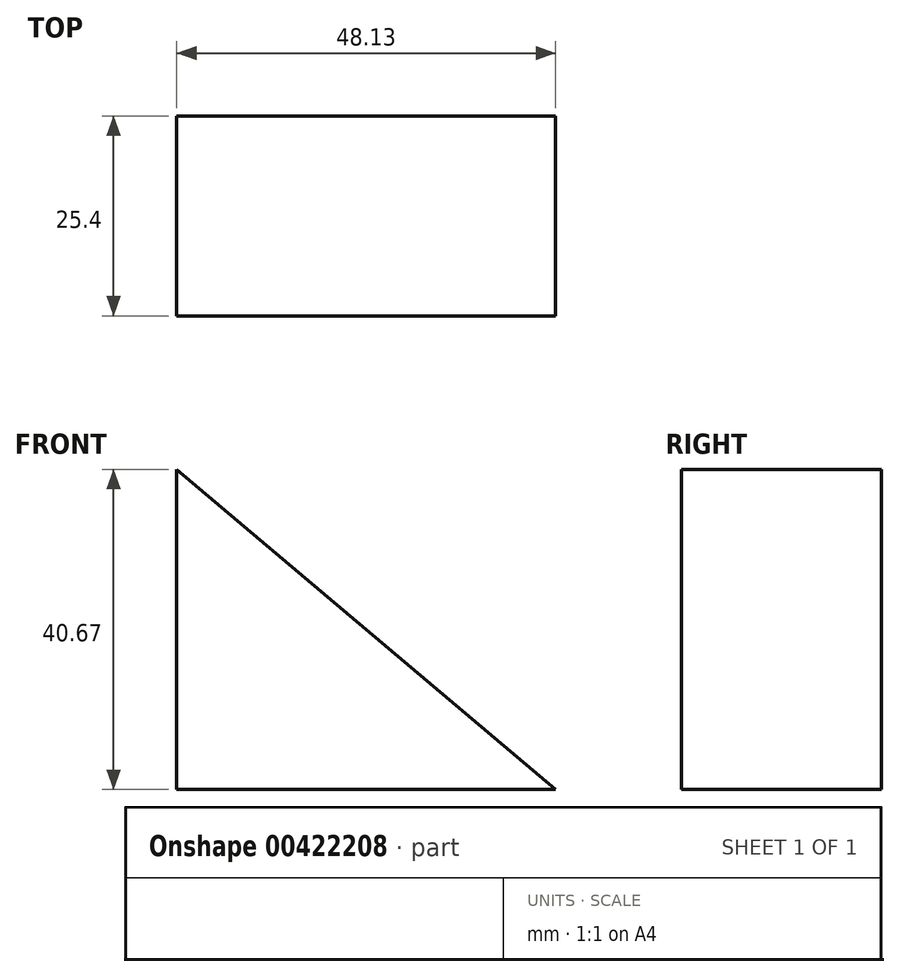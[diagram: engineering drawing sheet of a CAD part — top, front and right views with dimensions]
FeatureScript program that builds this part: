
annotation { "Feature Type Name" : "Feature", "Feature Type Description" : "" }
export const myFeature = defineFeature(function(context is Context, id is Id, definition is map)
    precondition{}
    {
        {
            var Q0;
            Q0=qCreatedBy(makeId("Front.planeOp"),FACE);
            var sketch = newSketch(context, id + "F0", { "sketchPlane" : qUnion([Q0])});
            skLineSegment(sketch, "E0", {"start": v(-40.48, 53.46) * mm, "end": v(-40.48, 12.8) * mm});
            skLineSegment(sketch, "E1", {"start": v(-40.48, 12.8) * mm, "end": v(7.65, 12.8) * mm});
            skLineSegment(sketch, "E2", {"start": v(7.65, 12.8) * mm, "end": v(-40.48, 53.46) * mm});
            skSolve(sketch);
        }
        {
            var Q0;
            Q0=makeQuery(id+"F0.imprint","IMPRINT",FACE,{"disambiguationData":[TD([[makeQuery(id+"F0.imprint","IMPRINT",EDGE,{"derivedFrom":sQuery(id+"F0.wireOp",EDGE,"E0")}),1.0]])]});
            extrude(context, id + "F1", {"entities" : qUnion([Q0]), "depth" : 25.4 * mm});
        }
    });
